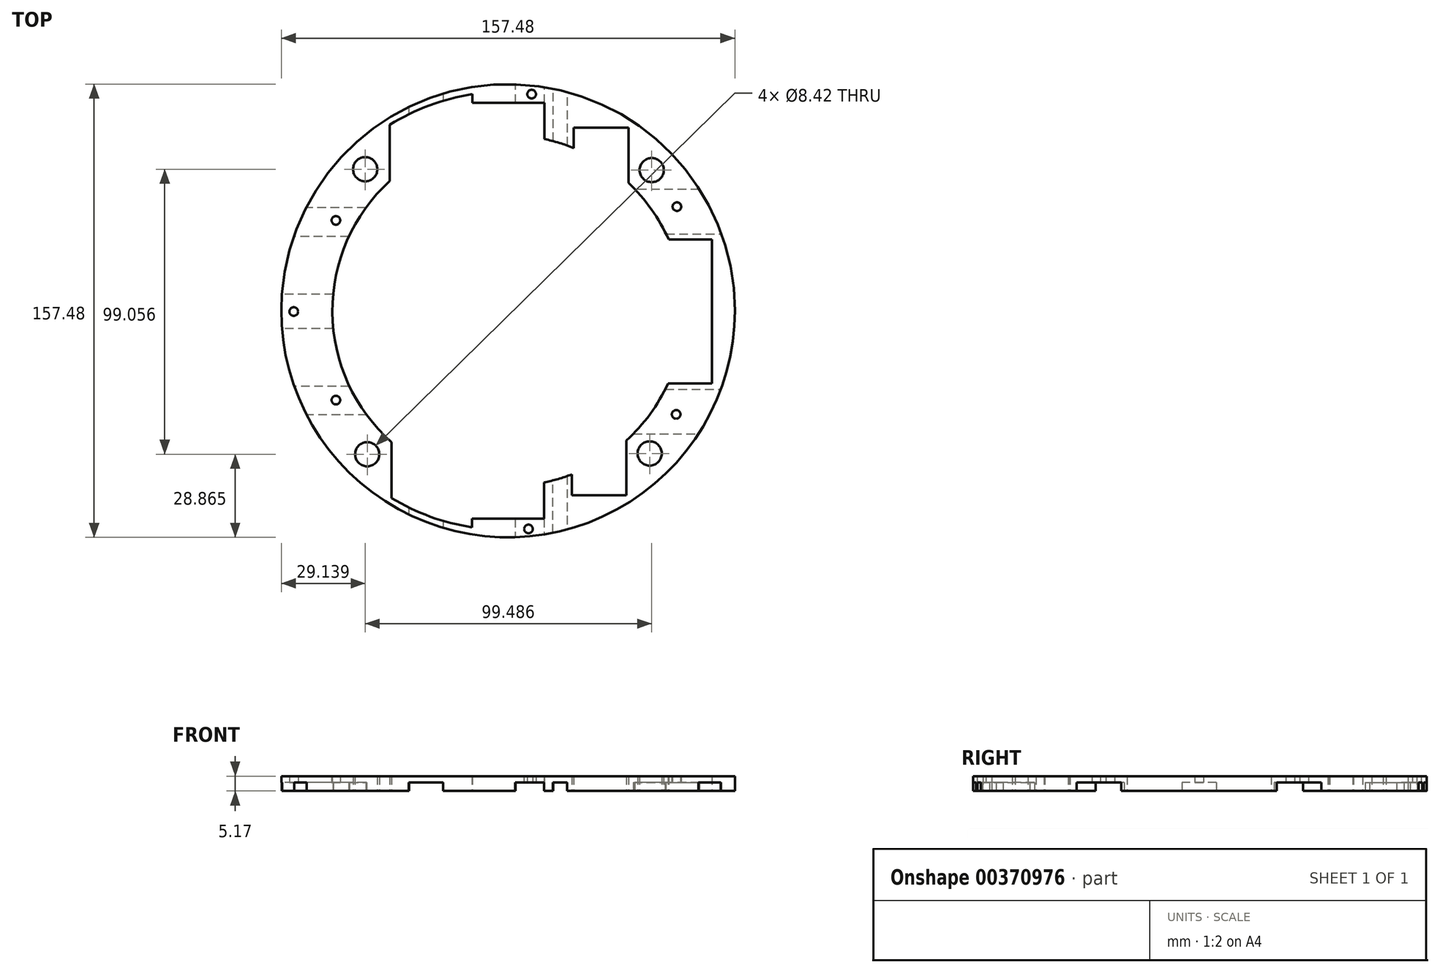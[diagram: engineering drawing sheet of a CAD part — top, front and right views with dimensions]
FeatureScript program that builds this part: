
annotation { "Feature Type Name" : "Feature", "Feature Type Description" : "" }
export const myFeature = defineFeature(function(context is Context, id is Id, definition is map)
    precondition{}
    {
        {
            var Q0;
            Q0=qCreatedBy(makeId("Top.planeOp"),FACE);
            var sketch = newSketch(context, id + "F0", { "sketchPlane" : qUnion([Q0])});
            skCircle(sketch, "E0", {"center": v(-0.13, 0.27) * mm, "radius": 78.74 * mm});
            skCircle(sketch, "E1", {"center": v(-0.13, 0.27) * mm, "radius": 61 * mm});
            skCircle(sketch, "E2", {"center": v(49.06, -49.32) * mm, "radius": 4.2 * mm});
            skCircle(sketch, "E3", {"center": v(-49.03, -49.6) * mm, "radius": 4.2 * mm});
            skCircle(sketch, "E4", {"center": v(-49.73, 49.45) * mm, "radius": 4.2 * mm});
            skCircle(sketch, "E5", {"center": v(49.76, 49.17) * mm, "radius": 4.2 * mm});
            skLineSegment(sketch, "E6", {"start": v(0, 0) * mm, "end": v(0, 79.01) * mm, "construction": true});
            skLineSegment(sketch, "E7", {"start": v(0, 72.51) * mm, "end": v(12.5, 72.51) * mm});
            skLineSegment(sketch, "E8", {"start": v(12.5, 72.51) * mm, "end": v(12.5, 59.95) * mm});
            skLineSegment(sketch, "E9", {"start": v(0, 72.51) * mm, "end": v(-12.5, 72.51) * mm});
            skLineSegment(sketch, "E10", {"start": v(-12.5, 72.51) * mm, "end": v(-12.5, 60) * mm});
            skLineSegment(sketch, "E11", {"start": v(12.37, -59.43) * mm, "end": v(12.37, -71.97) * mm});
            skLineSegment(sketch, "E12", {"start": v(12.37, -71.97) * mm, "end": v(-12.63, -71.97) * mm});
            skLineSegment(sketch, "E13", {"start": v(-12.63, -71.97) * mm, "end": v(-12.63, -59.43) * mm});
            skLineSegment(sketch, "E14", {"start": v(-0.13, 0.27) * mm, "end": v(-0.13, -78.47) * mm, "construction": true});
            skLineSegment(sketch, "E15", {"start": v(55.64, 25) * mm, "end": v(70.61, 25) * mm});
            skLineSegment(sketch, "E16", {"start": v(70.61, 25) * mm, "end": v(70.61, -25) * mm});
            skLineSegment(sketch, "E17", {"start": v(70.61, -25) * mm, "end": v(55.4, -25) * mm});
            skLineSegment(sketch, "E18", {"start": v(41.66, 44.71) * mm, "end": v(41.66, 63.86) * mm});
            skLineSegment(sketch, "E19", {"start": v(22.66, 56.86) * mm, "end": v(22.66, 63.86) * mm});
            skLineSegment(sketch, "E20", {"start": v(22.66, 63.86) * mm, "end": v(41.66, 63.86) * mm});
            skLineSegment(sketch, "E21", {"start": v(40.96, -44.81) * mm, "end": v(40.96, -63.8) * mm});
            skLineSegment(sketch, "E22", {"start": v(40.96, -63.8) * mm, "end": v(21.96, -63.8) * mm});
            skLineSegment(sketch, "E23", {"start": v(21.96, -63.8) * mm, "end": v(21.96, -56.59) * mm});
            skLineSegment(sketch, "E24", {"start": v(-41.23, 45.34) * mm, "end": v(-41.23, 64.93) * mm});
            skLineSegment(sketch, "E25", {"start": v(-40.53, -45.43) * mm, "end": v(-40.53, -64.81) * mm});
            skLineSegment(sketch, "E26", {"start": v(-12.5, 72.51) * mm, "end": v(-12.5, 75.54) * mm});
            skLineSegment(sketch, "E27", {"start": v(-12.5, 75.54) * mm, "end": v(-12.5, 78.04) * mm, "construction": true});
            skLineSegment(sketch, "E28", {"start": v(-41.23, 64.93) * mm, "end": v(-41.23, 67.43) * mm, "construction": true});
            skLineSegment(sketch, "E29", {"start": v(-12.63, -71.97) * mm, "end": v(-12.63, -74.97) * mm});
            skLineSegment(sketch, "E30", {"start": v(-12.63, -74.97) * mm, "end": v(-12.63, -77.47) * mm, "construction": true});
            skLineSegment(sketch, "E31", {"start": v(-40.53, -64.81) * mm, "end": v(-40.53, -67.31) * mm, "construction": true});
            skArc(sketch, "E32", {"start": v(-12.5, 75.54) * mm, "mid": v(-27.39, 71.65) * mm, "end": v(-41.23, 64.93) * mm});
            skArc(sketch, "E33", {"start": v(-40.53, -64.81) * mm, "mid": v(-27.1, -71.3) * mm, "end": v(-12.63, -74.97) * mm});
            skSolve(sketch);
        }
        {
            var Q0;
            Q0=makeQuery(id+"F0.imprint","IMPRINT",FACE,{"disambiguationData":[TD([[makeQuery(id+"F0.imprint","IMPRINT",EDGE,{"derivedFrom":sQuery(id+"F0.wireOp",EDGE,"E0")}),1.0]])]});
            extrude(context, id + "F1", {"entities" : qUnion([Q0]), "depth" : 5.17 * mm});
        }
        {
            var Q0;
            Q0=makeQuery(id+"F1.opExtrude","CAP_FACE",FACE,{"disambiguationData":[OSD([sQuery(id+"F0.wireOp",EDGE,"E0"),sQuery(id+"F0.wireOp",EDGE,"E1"),sQuery(id+"F0.wireOp",EDGE,"E2"),sQuery(id+"F0.wireOp",EDGE,"E3"),sQuery(id+"F0.wireOp",EDGE,"E4"),sQuery(id+"F0.wireOp",EDGE,"E5"),sQuery(id+"F0.wireOp",EDGE,"E7"),sQuery(id+"F0.wireOp",EDGE,"E8"),sQuery(id+"F0.wireOp",EDGE,"E9"),sQuery(id+"F0.wireOp",EDGE,"E10"),sQuery(id+"F0.wireOp",EDGE,"E11"),sQuery(id+"F0.wireOp",EDGE,"E12"),sQuery(id+"F0.wireOp",EDGE,"E13"),sQuery(id+"F0.wireOp",EDGE,"E15"),sQuery(id+"F0.wireOp",EDGE,"E16"),sQuery(id+"F0.wireOp",EDGE,"E17"),sQuery(id+"F0.wireOp",EDGE,"VDoqfpsv-4qcT-wrSo-6fLa-toxSMHrRfi2n"),sQuery(id+"F0.wireOp",EDGE,"kHyOE8iL-SrmW-cCEl-JhYE-iEjDphq27qqo"),sQuery(id+"F0.wireOp",EDGE,"IaEaYM1Z-oLR1-5D0C-0tBp-6euCYm71ufNU"),sQuery(id+"F0.wireOp",EDGE,"CqAKj5as-z6O8-Euua-ijw3-IaK4U2F1WzIA"),sQuery(id+"F0.wireOp",EDGE,"bdrpM5pd-59yM-zCnh-CLfW-zA1UQOxDqrim"),sQuery(id+"F0.wireOp",EDGE,"NGnk7T17-qjil-4RGJ-5A7U-nu3JMBgdJVSq")])],"isStart":true});
            var sketch = newSketch(context, id + "F2", { "sketchPlane" : qUnion([Q0])});
            skLineSegment(sketch, "E34", {"start": v(-49.2, 35.94) * mm, "end": v(-70.04, 35.94) * mm});
            skLineSegment(sketch, "E35", {"start": v(-55.2, 25.94) * mm, "end": v(-74.37, 25.94) * mm});
            skLineSegment(sketch, "E36", {"start": v(-22.63, 72.77) * mm, "end": v(-22.63, 75.18) * mm});
            skLineSegment(sketch, "E37", {"start": v(-34.63, 68.08) * mm, "end": v(-34.63, 70.5) * mm});
            skLineSegment(sketch, "E38", {"start": v(-55.4, -26.06) * mm, "end": v(-74.53, -26.06) * mm});
            skLineSegment(sketch, "E39", {"start": v(-49.53, -36.06) * mm, "end": v(-70.27, -36.06) * mm});
            skLineSegment(sketch, "E40", {"start": v(-22.5, -73.28) * mm, "end": v(-22.5, -75.77) * mm});
            skLineSegment(sketch, "E41", {"start": v(-34.5, -68.62) * mm, "end": v(-34.5, -71.11) * mm});
            skLineSegment(sketch, "E42", {"start": v(-60.85, -6.06) * mm, "end": v(-78.65, -6.06) * mm});
            skLineSegment(sketch, "E43", {"start": v(-60.8, 5.94) * mm, "end": v(-78.62, 5.94) * mm});
            skLineSegment(sketch, "E44", {"start": v(12.5, -72.51) * mm, "end": v(12.5, -78) * mm});
            skLineSegment(sketch, "E45", {"start": v(2.5, -72.51) * mm, "end": v(2.5, -78.97) * mm});
            skLineSegment(sketch, "E46", {"start": v(12.37, 71.97) * mm, "end": v(12.37, 77.47) * mm});
            skLineSegment(sketch, "E47", {"start": v(2.37, 71.97) * mm, "end": v(2.37, 78.43) * mm});
            skLineSegment(sketch, "E48", {"start": v(20.37, 57.18) * mm, "end": v(20.37, 75.75) * mm});
            skLineSegment(sketch, "E49", {"start": v(15.37, 76.93) * mm, "end": v(15.37, 58.72) * mm});
            skLineSegment(sketch, "E50", {"start": v(20.5, -57.68) * mm, "end": v(20.5, -76.26) * mm});
            skLineSegment(sketch, "E51", {"start": v(15.5, -59.24) * mm, "end": v(15.5, -77.45) * mm});
            skLineSegment(sketch, "E52", {"start": v(54.7, -27) * mm, "end": v(73.94, -27) * mm});
            skLineSegment(sketch, "E53", {"start": v(54.44, 27) * mm, "end": v(73.74, 27) * mm});
            skLineSegment(sketch, "E54", {"start": v(66.33, -42.5) * mm, "end": v(43.9, -42.5) * mm});
            skLineSegment(sketch, "E55", {"start": v(43.36, 42.5) * mm, "end": v(65.98, 42.5) * mm});
            skSolve(sketch);
        }
        {
            var Q0;
            {var subQ0=sQuery(id+"F2.wireOp",EDGE,"E36");Q0=makeQuery(id+"F2.imprint","IMPRINT",FACE,{"disambiguationData":[TD([[makeQuery(id+"F2.imprint","IMPRINT",EDGE,{"derivedFrom":subQ0}),1.0]])]});}
            var Q1;
            {var subQ0=sQuery(id+"F2.wireOp",EDGE,"qSOFF5Qn-LBtT-ckb4-KCcS-4EMrhRVFEw5l");Q1=makeQuery(id+"F2.imprint","IMPRINT",FACE,{"disambiguationData":[TD([[makeQuery(id+"F2.imprint","IMPRINT",EDGE,{"derivedFrom":subQ0}),-1.0]])]});}
            var Q2;
            {var subQ0=sQuery(id+"F2.wireOp",EDGE,"q6fSSL3S-2UqV-hRAR-x4fO-Y75Hsksp0FtS");Q2=makeQuery(id+"F2.imprint","IMPRINT",FACE,{"disambiguationData":[TD([[makeQuery(id+"F2.imprint","IMPRINT",EDGE,{"derivedFrom":subQ0}),1.0]])]});}
            var Q3;
            {var subQ0=sQuery(id+"F2.wireOp",EDGE,"E40");Q3=makeQuery(id+"F2.imprint","IMPRINT",FACE,{"disambiguationData":[TD([[makeQuery(id+"F2.imprint","IMPRINT",EDGE,{"derivedFrom":subQ0}),-1.0]])]});}
            var Q4;
            {var subQ0=sQuery(id+"F2.wireOp",EDGE,"E38");Q4=makeQuery(id+"F2.imprint","IMPRINT",FACE,{"disambiguationData":[TD([[makeQuery(id+"F2.imprint","IMPRINT",EDGE,{"derivedFrom":subQ0}),1.0]])]});}
            var Q5;
            {var subQ0=sQuery(id+"F2.wireOp",EDGE,"E42");Q5=makeQuery(id+"F2.imprint","IMPRINT",FACE,{"disambiguationData":[TD([[makeQuery(id+"F2.imprint","IMPRINT",EDGE,{"derivedFrom":subQ0}),-1.0]])]});}
            var Q6;
            {var subQ0=sQuery(id+"F2.wireOp",EDGE,"E34");Q6=makeQuery(id+"F2.imprint","IMPRINT",FACE,{"disambiguationData":[TD([[makeQuery(id+"F2.imprint","IMPRINT",EDGE,{"derivedFrom":subQ0}),1.0]])]});}
            var Q7;
            {var subQ0=sQuery(id+"F2.wireOp",EDGE,"E44");Q7=makeQuery(id+"F2.imprint","IMPRINT",FACE,{"disambiguationData":[TD([[makeQuery(id+"F2.imprint","IMPRINT",EDGE,{"derivedFrom":subQ0}),-1.0]])]});}
            var Q8;
            {var subQ0=sQuery(id+"F2.wireOp",EDGE,"E46");Q8=makeQuery(id+"F2.imprint","IMPRINT",FACE,{"disambiguationData":[TD([[makeQuery(id+"F2.imprint","IMPRINT",EDGE,{"derivedFrom":subQ0}),1.0]])]});}
            var Q9;
            {var subQ0=sQuery(id+"F2.wireOp",EDGE,"3tUUMQLs-xen7-DnnY-Bd8B-tcTG2vnb8p7U");Q9=makeQuery(id+"F2.imprint","IMPRINT",FACE,{"disambiguationData":[TD([[makeQuery(id+"F2.imprint","IMPRINT",EDGE,{"derivedFrom":subQ0}),-1.0]])]});}
            var Q10;
            {var subQ0=sQuery(id+"F2.wireOp",EDGE,"E48");Q10=makeQuery(id+"F2.imprint","IMPRINT",FACE,{"disambiguationData":[TD([[makeQuery(id+"F2.imprint","IMPRINT",EDGE,{"derivedFrom":subQ0}),1.0]])]});}
            var Q11;
            {var subQ0=sQuery(id+"F2.wireOp",EDGE,"E50");Q11=makeQuery(id+"F2.imprint","IMPRINT",FACE,{"disambiguationData":[TD([[makeQuery(id+"F2.imprint","IMPRINT",EDGE,{"derivedFrom":subQ0}),-1.0]])]});}
            var Q12;
            {var subQ0=sQuery(id+"F2.wireOp",EDGE,"E52");Q12=makeQuery(id+"F2.imprint","IMPRINT",FACE,{"disambiguationData":[TD([[makeQuery(id+"F2.imprint","IMPRINT",EDGE,{"derivedFrom":subQ0}),-1.0]])]});}
            var Q13;
            {var subQ0=sQuery(id+"F2.wireOp",EDGE,"E53");Q13=makeQuery(id+"F2.imprint","IMPRINT",FACE,{"disambiguationData":[TD([[makeQuery(id+"F2.imprint","IMPRINT",EDGE,{"derivedFrom":subQ0}),1.0]])]});}
            extrude(context, id + "F3", {"entities" : qUnion([Q0, Q1, Q2, Q3, Q4, Q5, Q6, Q7, Q8, Q9, Q10, Q11, Q12, Q13]), "operationType" : NewBodyOperationType.REMOVE, "oppositeDirection" : true, "depth" : 3 * mm});
        }
        {
            var Q0;
            Q0=makeQuery(id+"F3.boolean.opBoolean","COPY",FACE,{"derivedFrom":makeQuery(id+"F3.opExtrude","CAP_FACE",FACE,{"disambiguationData":[OSD([sQuery(id+"F0.wireOp",EDGE,"E0"),sQuery(id+"F0.wireOp",EDGE,"E1"),sQuery(id+"F2.wireOp",EDGE,"E38"),sQuery(id+"F2.wireOp",EDGE,"E39")])],"isStart":false})});
            var sketch = newSketch(context, id + "F4", { "sketchPlane" : qUnion([Q0])});
            skCircle(sketch, "E56", {"center": v(-59.9, -31.68) * mm, "radius": 1.5 * mm});
            skPoint(sketch, "E56.centerSnap0", {"position": v(-59.9, -36.06) * mm});
            skCircle(sketch, "E57", {"center": v(-59.9, 30.79) * mm, "radius": 1.5 * mm});
            skCircle(sketch, "E58", {"center": v(8.06, -75.57) * mm, "radius": 1.5 * mm});
            skCircle(sketch, "E59", {"center": v(58.5, -36.47) * mm, "radius": 1.5 * mm});
            skCircle(sketch, "E60", {"center": v(58.24, 35.74) * mm, "radius": 1.5 * mm});
            skCircle(sketch, "E61", {"center": v(6.96, 75.56) * mm, "radius": 1.5 * mm});
            skCircle(sketch, "E62", {"center": v(-74.53, 0) * mm, "radius": 1.5 * mm});
            skSolve(sketch);
        }
        {
            var Q0;
            Q0=makeQuery(id+"F4.imprint","IMPRINT",FACE,{"disambiguationData":[TD([[makeQuery(id+"F4.imprint","IMPRINT",EDGE,{"derivedFrom":sQuery(id+"F4.wireOp",EDGE,"E62")}),1.0]])]});
            var Q1;
            Q1=makeQuery(id+"F4.imprint","IMPRINT",FACE,{"disambiguationData":[TD([[makeQuery(id+"F4.imprint","IMPRINT",EDGE,{"derivedFrom":sQuery(id+"F4.wireOp",EDGE,"E57")}),1.0]])]});
            var Q2;
            Q2=makeQuery(id+"F4.imprint","IMPRINT",FACE,{"disambiguationData":[TD([[makeQuery(id+"F4.imprint","IMPRINT",EDGE,{"derivedFrom":sQuery(id+"F4.wireOp",EDGE,"E56")}),1.0]])]});
            var Q3;
            Q3=makeQuery(id+"F4.imprint","IMPRINT",FACE,{"disambiguationData":[TD([[makeQuery(id+"F4.imprint","IMPRINT",EDGE,{"derivedFrom":sQuery(id+"F4.wireOp",EDGE,"E58")}),1.0]])]});
            var Q4;
            Q4=makeQuery(id+"F4.imprint","IMPRINT",FACE,{"disambiguationData":[TD([[makeQuery(id+"F4.imprint","IMPRINT",EDGE,{"derivedFrom":sQuery(id+"F4.wireOp",EDGE,"a8RiTg22-5cp5-0Lyg-D3pn-yzNnpAkmeHB0")}),1.0]])]});
            var Q5;
            Q5=makeQuery(id+"F4.imprint","IMPRINT",FACE,{"disambiguationData":[TD([[makeQuery(id+"F4.imprint","IMPRINT",EDGE,{"derivedFrom":sQuery(id+"F4.wireOp",EDGE,"HCF0FYdm-k2oz-RcCJ-R9aZ-c2gy1UOGrMCM")}),1.0]])]});
            var Q6;
            Q6=makeQuery(id+"F4.imprint","IMPRINT",FACE,{"disambiguationData":[TD([[makeQuery(id+"F4.imprint","IMPRINT",EDGE,{"derivedFrom":sQuery(id+"F4.wireOp",EDGE,"E61")}),1.0]])]});
            var Q7;
            Q7=makeQuery(id+"F4.imprint","IMPRINT",FACE,{"disambiguationData":[TD([[makeQuery(id+"F4.imprint","IMPRINT",EDGE,{"derivedFrom":sQuery(id+"F4.wireOp",EDGE,"E60")}),1.0]])]});
            var Q8;
            Q8=makeQuery(id+"F4.imprint","IMPRINT",FACE,{"disambiguationData":[TD([[makeQuery(id+"F4.imprint","IMPRINT",EDGE,{"derivedFrom":sQuery(id+"F4.wireOp",EDGE,"E59")}),1.0]])]});
            extrude(context, id + "F5", {"entities" : qUnion([Q0, Q1, Q2, Q3, Q4, Q5, Q6, Q7, Q8]), "operationType" : NewBodyOperationType.REMOVE, "oppositeDirection" : true, "depth" : 25 * mm});
        }
    });
